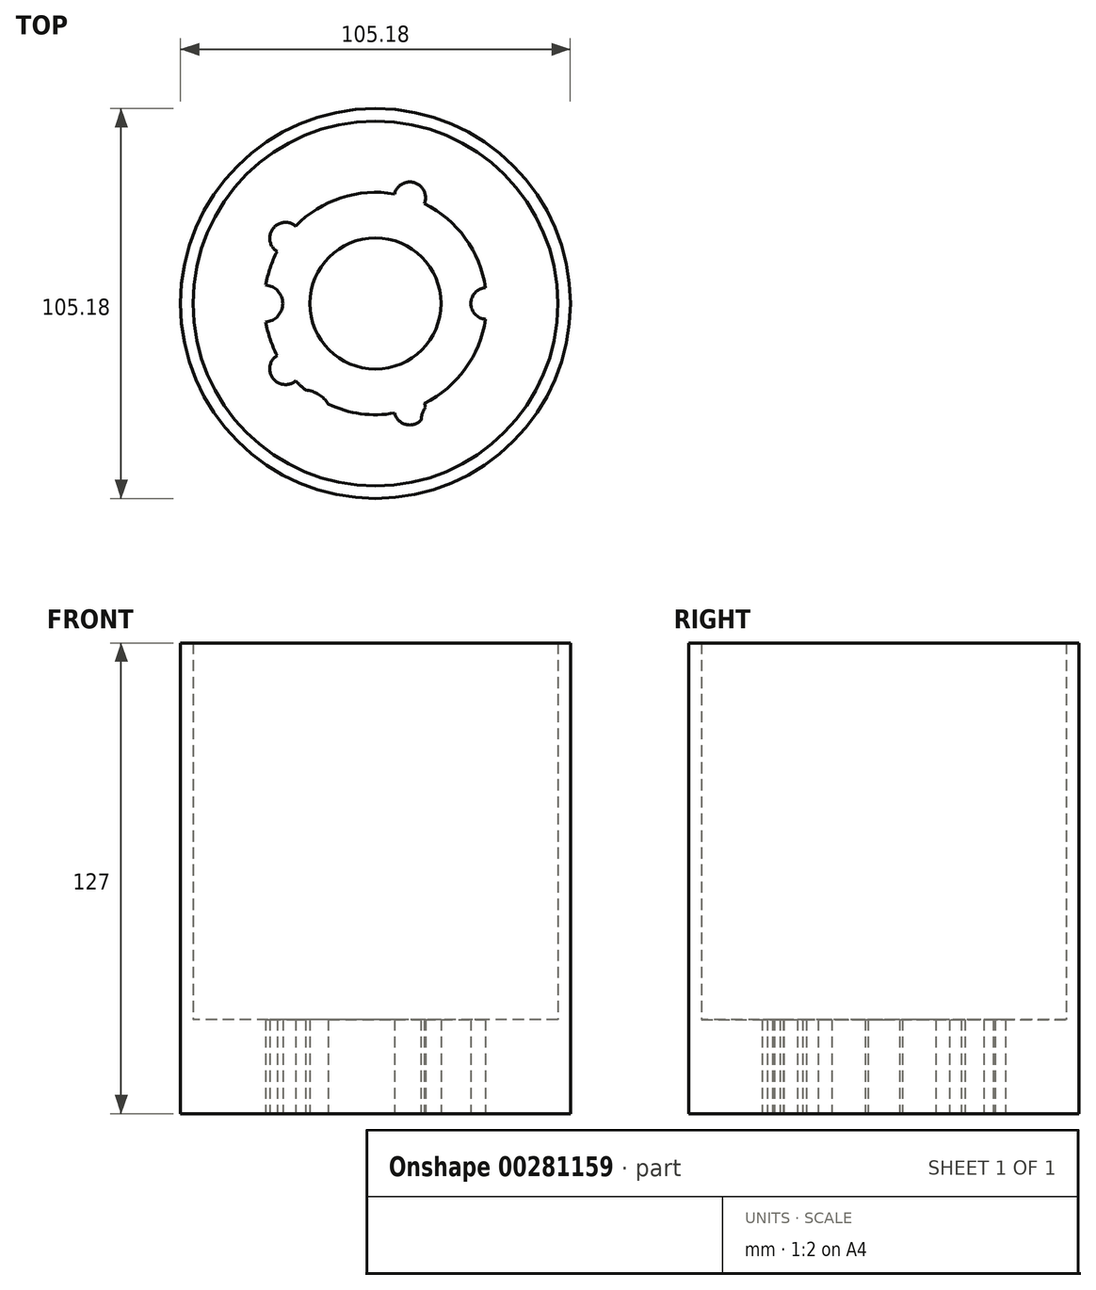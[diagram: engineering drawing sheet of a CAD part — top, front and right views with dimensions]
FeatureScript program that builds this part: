
annotation { "Feature Type Name" : "Feature", "Feature Type Description" : "" }
export const myFeature = defineFeature(function(context is Context, id is Id, definition is map)
    precondition{}
    {
        {
            var Q0;
            Q0=qCreatedBy(makeId("Top.planeOp"),FACE);
            var sketch = newSketch(context, id + "F0", { "sketchPlane" : qUnion([Q0])});
            skCircle(sketch, "E0", {"center": v(0, 0) * mm, "radius": 52.6 * mm});
            skCircle(sketch, "E1", {"center": v(0, 0) * mm, "radius": 49.22 * mm});
            skCircle(sketch, "E2", {"center": v(30, 0) * mm, "radius": 4.25 * mm});
            skCircle(sketch, "E3", {"center": v(-19.64, -31.48) * mm, "radius": 8.17 * mm});
            skCircle(sketch, "E4", {"center": v(18.87, -31.68) * mm, "radius": 6.55 * mm});
            skCircle(sketch, "E5", {"center": v(-30, 0) * mm, "radius": 5 * mm});
            skCircle(sketch, "E6", {"center": v(0, 0) * mm, "radius": 30 * mm});
            skCircle(sketch, "E7.1.1", {"center": v(9.27, 28.53) * mm, "radius": 4.25 * mm});
            skCircle(sketch, "E7.2.1", {"center": v(-24.27, 17.63) * mm, "radius": 4.25 * mm});
            skCircle(sketch, "E7.3.1", {"center": v(-24.27, -17.63) * mm, "radius": 4.25 * mm});
            skCircle(sketch, "E7.4.1", {"center": v(9.27, -28.53) * mm, "radius": 4.25 * mm});
            skLineSegment(sketch, "E7.anchor1", {"start": v(0, 0) * mm, "end": v(30, 0) * mm, "construction": true});
            skLineSegment(sketch, "E7.anchor2", {"start": v(0, 0) * mm, "end": v(9.27, -28.53) * mm, "construction": true});
            skSolve(sketch);
        }
        {
            var Q0;
            Q0=qCreatedBy(makeId("Top.planeOp"),FACE);
            var sketch = newSketch(context, id + "F1", { "sketchPlane" : qUnion([Q0])});
            skCircle(sketch, "E8", {"center": v(0, 0) * mm, "radius": 17.69 * mm});
            skSolve(sketch);
        }
        {
            var Q0;
            Q0=makeQuery(id+"F0.imprint","IMPRINT",FACE,{"disambiguationData":[TD([[makeQuery(id+"F0.imprint","IMPRINT",EDGE,{"derivedFrom":sQuery(id+"F0.wireOp",EDGE,"eoMLtNo1-gEf7-mG1I-rBLj-b4IeXRFsLGdL")}),1.0]])]});
            var sketch = newSketch(context, id + "F2", { "sketchPlane" : qUnion([Q0])});
            skSolve(sketch);
        }
        {
            var Q0;
            Q0=makeQuery(id+"F0.imprint","IMPRINT",FACE,{"disambiguationData":[TD([[makeQuery(id+"F0.imprint","IMPRINT",EDGE,{"derivedFrom":sQuery(id+"F0.wireOp",EDGE,"eoMLtNo1-gEf7-mG1I-rBLj-b4IeXRFsLGdL")}),1.0]])]});
            var Q1;
            Q1=makeQuery(id+"F0.imprint","IMPRINT",FACE,{"disambiguationData":[TD([[makeQuery(id+"F0.imprint","IMPRINT",EDGE,{"derivedFrom":sQuery(id+"F0.wireOp",EDGE,"CirVUKhY-aqoX-VEPj-rrlA-51o3HWx39UIJ")}),1.0]])]});
            var Q2;
            Q2=makeQuery(id+"F0.imprint","IMPRINT",FACE,{"disambiguationData":[TD([[makeQuery(id+"F0.imprint","IMPRINT",EDGE,{"derivedFrom":sQuery(id+"F0.wireOp",EDGE,"E5")}),1.0]])]});
            var Q3;
            Q3=makeQuery(id+"F0.imprint","IMPRINT",FACE,{"disambiguationData":[TD([[makeQuery(id+"F0.imprint","IMPRINT",EDGE,{"derivedFrom":sQuery(id+"F0.wireOp",EDGE,"E3")}),1.0]])]});
            var Q4;
            Q4=makeQuery(id+"F0.imprint","IMPRINT",FACE,{"disambiguationData":[TD([[makeQuery(id+"F0.imprint","IMPRINT",EDGE,{"derivedFrom":sQuery(id+"F0.wireOp",EDGE,"E4")}),1.0]])]});
            var Q5;
            Q5=makeQuery(id+"F0.imprint","IMPRINT",FACE,{"disambiguationData":[TD([[makeQuery(id+"F0.imprint","IMPRINT",EDGE,{"derivedFrom":sQuery(id+"F0.wireOp",EDGE,"E2")}),1.0]])]});
            extrude(context, id + "F3", {"entities" : qUnion([Q0, Q1, Q2, Q3, Q4, Q5]), "depth" : 25.4 * mm});
        }
        {
            var Q0;
            Q0=makeQuery(id+"F0.imprint","IMPRINT",FACE,{"disambiguationData":[TD([[makeQuery(id+"F0.imprint","IMPRINT",EDGE,{"derivedFrom":sQuery(id+"F0.wireOp",EDGE,"E1")}),1.0]])]});
            var sketch = newSketch(context, id + "F4", { "sketchPlane" : qUnion([Q0])});
            skSolve(sketch);
        }
        {
            var Q0;
            Q0=makeQuery(id+"F0.imprint","IMPRINT",FACE,{"disambiguationData":[TD([[makeQuery(id+"F0.imprint","IMPRINT",EDGE,{"derivedFrom":sQuery(id+"F0.wireOp",EDGE,"E0")}),1.0]])]});
            var sketch = newSketch(context, id + "F5", { "sketchPlane" : qUnion([Q0])});
            skSolve(sketch);
        }
        {
            var Q0;
            Q0=makeQuery(id+"F0.imprint","IMPRINT",FACE,{"disambiguationData":[TD([[makeQuery(id+"F0.imprint","IMPRINT",EDGE,{"derivedFrom":sQuery(id+"F0.wireOp",EDGE,"E1")}),1.0]])]});
            var Q1;
            Q1 = qSketchRegion(id + "F1", true);
            var Q2;
            Q2 = qSketchRegion(id + "F2", true);
            var Q3;
            Q3 = qSketchRegion(id + "F4", true);
            var Q4;
            Q4 = qSketchRegion(id + "F5", true);
            var Q5;
            Q5=sQuery(id+"F1.wireOp",EDGE,"E8");
            extrude(context, id + "F6", {"entities" : qUnion([Q0, Q1, Q2, Q3, Q4]), "surfaceEntities" : qUnion([Q5]), "depth" : 25.4 * mm});
        }
        {
            var Q0;
            Q0=makeQuery(id+"F0.imprint","IMPRINT",FACE,{"disambiguationData":[TD([[makeQuery(id+"F0.imprint","IMPRINT",EDGE,{"derivedFrom":sQuery(id+"F0.wireOp",EDGE,"E0")}),1.0]])]});
            var Q1;
            Q1=sQuery(id+"F0.wireOp",EDGE,"E0");
            var Q2;
            Q2=sQuery(id+"F0.wireOp",EDGE,"E1");
            extrude(context, id + "F7", {"entities" : qUnion([Q0]), "operationType" : NewBodyOperationType.ADD, "surfaceEntities" : qUnion([Q1, Q2]), "depth" : 127 * mm});
        }
        {
            var Q0;
            Q0=makeQuery(id+"F6.opExtrude","CAP_FACE",FACE,{"disambiguationData":[OSD([sQuery(id+"F0.wireOp",EDGE,"E1"),sQuery(id+"F0.wireOp",EDGE,"eoMLtNo1-gEf7-mG1I-rBLj-b4IeXRFsLGdL"),sQuery(id+"F0.wireOp",EDGE,"E2"),sQuery(id+"F0.wireOp",EDGE,"E3"),sQuery(id+"F0.wireOp",EDGE,"E4"),sQuery(id+"F0.wireOp",EDGE,"CirVUKhY-aqoX-VEPj-rrlA-51o3HWx39UIJ"),sQuery(id+"F0.wireOp",EDGE,"E5")])],"isStart":false});
            var sketch = newSketch(context, id + "F8", { "sketchPlane" : qUnion([Q0])});
            skSolve(sketch);
        }
        {
            var Q0;
            {var subQ0=sQuery(id+"F0.wireOp",EDGE,"E6");var subQ5=sQuery(id+"F0.wireOp",EDGE,"E2");var subQ9=makeQuery(id+"F0.imprint","INTERSECT",VERTEX,{"disambiguationData":[OD(0.0)],"derivedFrom":[subQ5,subQ0]});Q0=makeQuery(id+"F0.imprint","IMPRINT",FACE,{"disambiguationData":[TD([[makeQuery(id+"F0.imprint","IMPRINT",EDGE,{"disambiguationData":[TD([[subQ9,1.0]])],"derivedFrom":subQ5}),-1.0]])]});}
            var Q1;
            Q1=makeQuery(id+"F0.imprint","IMPRINT",FACE,{"disambiguationData":[TD([[makeQuery(id+"F0.imprint","IMPRINT",EDGE,{"derivedFrom":sQuery(id+"F0.wireOp",EDGE,"E1")}),1.0]])]});
            extrude(context, id + "F9", {"entities" : qUnion([Q0, Q1]), "operationType" : NewBodyOperationType.ADD, "depth" : 25 * mm});
        }
    });
